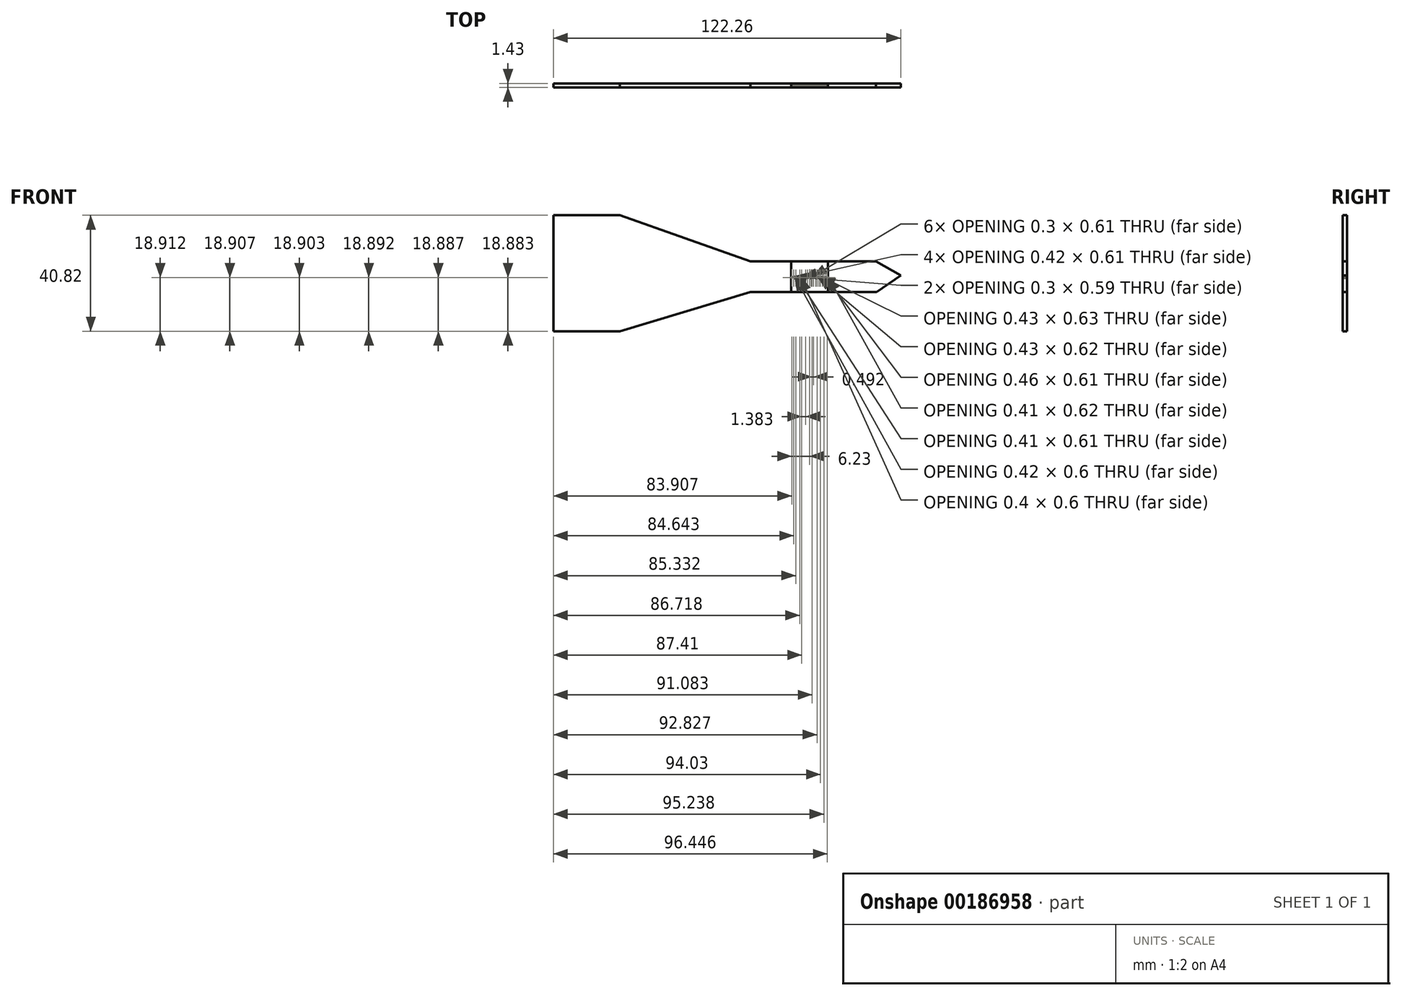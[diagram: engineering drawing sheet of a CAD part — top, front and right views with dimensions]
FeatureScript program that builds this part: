
annotation { "Feature Type Name" : "Feature", "Feature Type Description" : "" }
export const myFeature = defineFeature(function(context is Context, id is Id, definition is map)
    precondition{}
    {
        {
            var Q0;
            Q0=qCreatedBy(makeId("Front.planeOp"),FACE);
            var sketch = newSketch(context, id + "F0", { "sketchPlane" : qUnion([Q0])});
            skLineSegment(sketch, "E0", {"start": v(-45.9, 45.81) * mm, "end": v(0, 29.54) * mm});
            skLineSegment(sketch, "E1", {"start": v(-45.9, 5) * mm, "end": v(0, 18.72) * mm});
            skLineSegment(sketch, "E2", {"start": v(0, 29.54) * mm, "end": v(44.25, 29.54) * mm});
            skLineSegment(sketch, "E3", {"start": v(0, 18.72) * mm, "end": v(44.42, 18.72) * mm});
            skLineSegment(sketch, "E4", {"start": v(44.42, 18.72) * mm, "end": v(52.93, 24.67) * mm});
            skLineSegment(sketch, "E5", {"start": v(44.25, 29.54) * mm, "end": v(52.93, 24.67) * mm});
            skLineSegment(sketch, "E6", {"start": v(14.38, 29.54) * mm, "end": v(14.38, 18.72) * mm});
            skLineSegment(sketch, "E7", {"start": v(15.09, 29.54) * mm, "end": v(15.09, 18.72) * mm});
            skLineSegment(sketch, "E8", {"start": v(15.84, 29.54) * mm, "end": v(15.84, 18.72) * mm});
            skLineSegment(sketch, "E9", {"start": v(16.72, 29.54) * mm, "end": v(16.72, 18.72) * mm});
            skLineSegment(sketch, "E10", {"start": v(17.37, 29.54) * mm, "end": v(17.37, 18.72) * mm});
            skLineSegment(sketch, "E11", {"start": v(18.25, 29.54) * mm, "end": v(18.25, 18.72) * mm});
            skLineSegment(sketch, "E12", {"start": v(19.05, 29.54) * mm, "end": v(19.05, 18.72) * mm});
            skLineSegment(sketch, "E13", {"start": v(19.84, 29.54) * mm, "end": v(19.84, 18.72) * mm});
            skLineSegment(sketch, "E14", {"start": v(20.67, 29.54) * mm, "end": v(20.67, 18.72) * mm});
            skLineSegment(sketch, "E15", {"start": v(21.55, 29.54) * mm, "end": v(21.55, 18.72) * mm});
            skLineSegment(sketch, "E16", {"start": v(22.48, 29.54) * mm, "end": v(22.48, 18.72) * mm});
            skLineSegment(sketch, "E17", {"start": v(23.31, 29.54) * mm, "end": v(23.31, 18.72) * mm});
            skLineSegment(sketch, "E18", {"start": v(24.2, 29.54) * mm, "end": v(24.2, 18.72) * mm});
            skLineSegment(sketch, "E19", {"start": v(25.2, 29.54) * mm, "end": v(25.2, 18.72) * mm});
            skLineSegment(sketch, "E20", {"start": v(26.08, 29.54) * mm, "end": v(26.08, 18.72) * mm});
            skLineSegment(sketch, "E21", {"start": v(27.23, 29.54) * mm, "end": v(27.23, 18.72) * mm});
            skLineSegment(sketch, "E22", {"start": v(27.35, 29.57) * mm, "end": v(27.35, 18.72) * mm});
            skText(sketch, "E23", { "text": "1 2 3 4 5 6 7 8 9 10", "fontName": "OpenSans-Bold.ttf"});
            skText(sketch, "E24", { "text": "11 12 13 14 15", "fontName": "OpenSans-Bold.ttf"});
            skLineSegment(sketch, "E25", {"start": v(-45.9, 5) * mm, "end": v(-69.33, 5) * mm});
            skLineSegment(sketch, "E26", {"start": v(-45.9, 45.81) * mm, "end": v(-69.33, 45.81) * mm});
            skLineSegment(sketch, "E27", {"start": v(-69.33, 45.81) * mm, "end": v(-69.33, 5) * mm});
            const initialGuessF0  = {"E23": [0.01438, 0.0236, 1, 0, 0.0006], "E24": [0.02155, 0.02357, 1, 0, 0.00062]};
            skSetInitialGuess(sketch, initialGuessF0);
            skSolve(sketch);
        }
        {
            var Q0;
            {var subQ3=sQuery(id+"F0.wireOp",EDGE,"E0");Q0=makeQuery(id+"F0.imprint","IMPRINT",FACE,{"disambiguationData":[TD([[makeQuery(id+"F0.imprint","IMPRINT",EDGE,{"derivedFrom":subQ3}),-1.0]])]});}
            extrude(context, id + "F1", {"entities" : qUnion([Q0]), "depth" : 1.43 * mm});
        }
        {
            var Q0;
            Q0=sQuery(id+"F0.wireOp",EDGE,"E6");
            extrude(context, id + "F2", {"bodyType" : ToolBodyType.SURFACE, "surfaceEntities" : qUnion([Q0]), "depth" : 1.43 * mm});
        }
        {
            var Q0;
            Q0=sQuery(id+"F0.wireOp",EDGE,"E7");
            extrude(context, id + "F3", {"bodyType" : ToolBodyType.SURFACE, "surfaceEntities" : qUnion([Q0]), "depth" : 1.43 * mm});
        }
        {
            var Q0;
            Q0=sQuery(id+"F0.wireOp",EDGE,"E8");
            extrude(context, id + "F4", {"bodyType" : ToolBodyType.SURFACE, "surfaceEntities" : qUnion([Q0]), "depth" : 1.43 * mm});
        }
        {
            var Q0;
            Q0=sQuery(id+"F0.wireOp",EDGE,"E9");
            extrude(context, id + "F5", {"bodyType" : ToolBodyType.SURFACE, "surfaceEntities" : qUnion([Q0]), "depth" : 1.43 * mm});
        }
        {
            var Q0;
            Q0=sQuery(id+"F0.wireOp",EDGE,"E10");
            var Q1;
            Q1=sQuery(id+"F0.wireOp",EDGE,"E11");
            var Q2;
            Q2=sQuery(id+"F0.wireOp",EDGE,"E12");
            var Q3;
            Q3=sQuery(id+"F0.wireOp",EDGE,"E13");
            var Q4;
            Q4=sQuery(id+"F0.wireOp",EDGE,"E14");
            var Q5;
            Q5=sQuery(id+"F0.wireOp",EDGE,"E15");
            var Q6;
            Q6=sQuery(id+"F0.wireOp",EDGE,"E16");
            var Q7;
            Q7=sQuery(id+"F0.wireOp",EDGE,"E17");
            var Q8;
            Q8=sQuery(id+"F0.wireOp",EDGE,"E18");
            var Q9;
            Q9=sQuery(id+"F0.wireOp",EDGE,"E19");
            var Q10;
            Q10=sQuery(id+"F0.wireOp",EDGE,"E20");
            var Q11;
            Q11=sQuery(id+"F0.wireOp",EDGE,"E22");
            extrude(context, id + "F6", {"bodyType" : ToolBodyType.SURFACE, "surfaceEntities" : qUnion([Q0, Q1, Q2, Q3, Q4, Q5, Q6, Q7, Q8, Q9, Q10, Q11]), "depth" : 1.43 * mm});
        }
        {
            var Q0;
            {var subQ1=sQuery(id+"F0.wireOp",EDGE,"E4");Q0=makeQuery(id+"F0.imprint","IMPRINT",FACE,{"disambiguationData":[TD([[makeQuery(id+"F0.imprint","IMPRINT",EDGE,{"derivedFrom":subQ1}),1.0]])]});}
            extrude(context, id + "F7", {"entities" : qUnion([Q0]), "depth" : 1.43 * mm});
        }
        {
            var Q0;
            Q0 = qSketchRegion(id + "F0", true);
            extrude(context, id + "F8", {"entities" : qUnion([Q0]), "depth" : 1.43 * mm});
        }
    });
